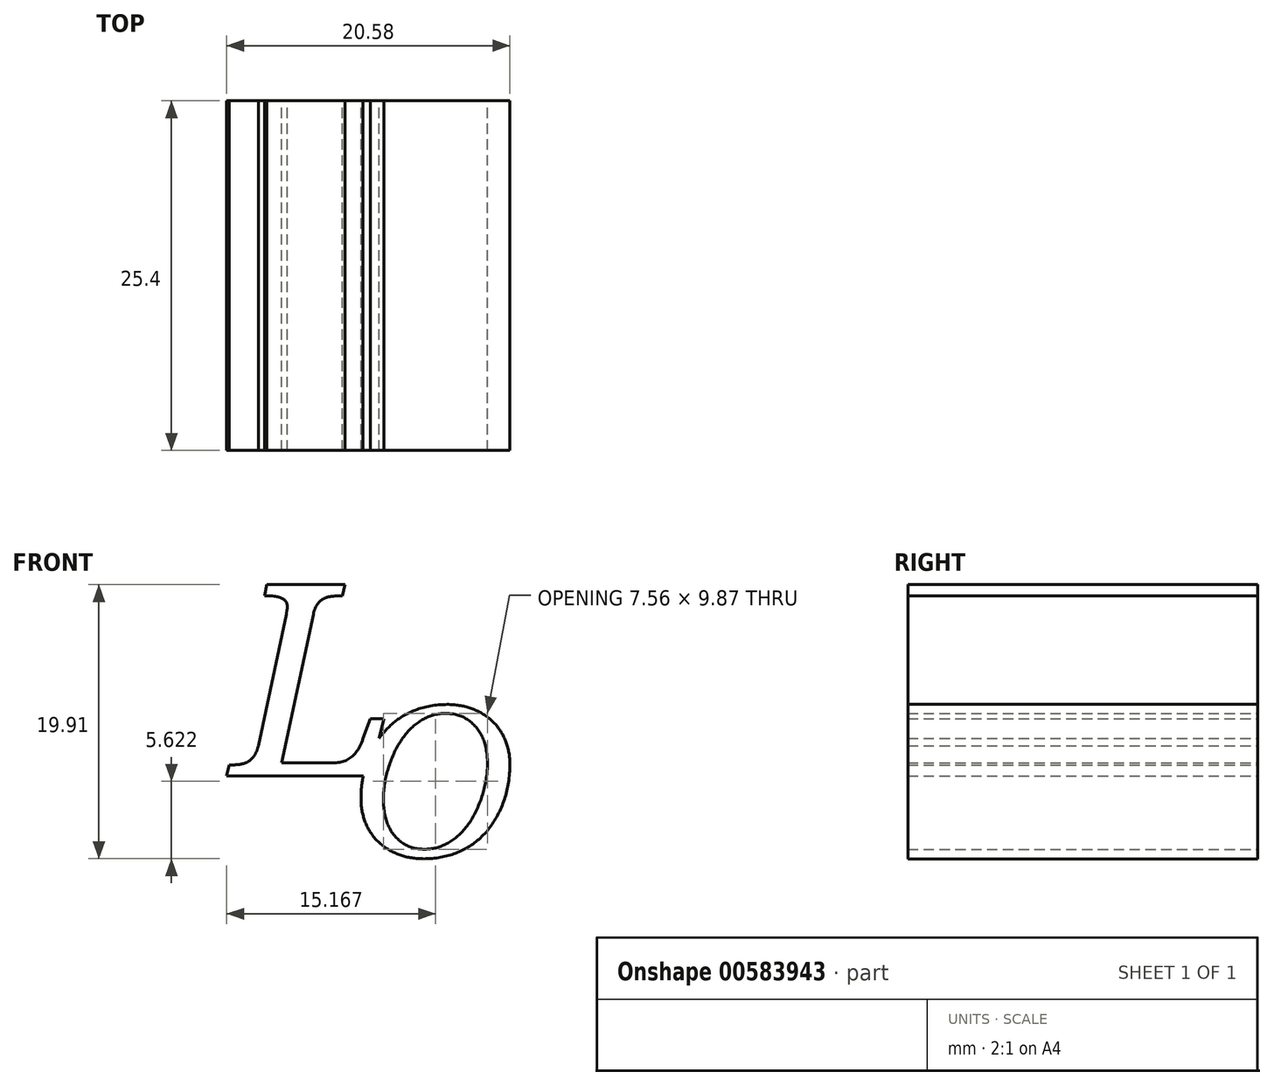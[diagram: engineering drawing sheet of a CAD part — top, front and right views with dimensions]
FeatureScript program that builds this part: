
annotation { "Feature Type Name" : "Feature", "Feature Type Description" : "" }
export const myFeature = defineFeature(function(context is Context, id is Id, definition is map)
    precondition{}
    {
        {
            var Q0;
            Q0=qCreatedBy(makeId("Front.planeOp"),FACE);
            var sketch = newSketch(context, id + "F0", { "sketchPlane" : qUnion([Q0])});
            skText(sketch, "E0", { "text": "L", "fontName": "NotoSerif-Italic.ttf"});
            const initialGuessF0  = {"E0": [-0.01286, -0.00168, 1, 0, 0.01403]};
            skSetInitialGuess(sketch, initialGuessF0);
            skSolve(sketch);
        }
        {
            var Q0;
            Q0=makeQuery(id+"F0.imprint","IMPRINT",FACE,{"disambiguationData":[TD([[makeQuery(id+"F0.imprint","IMPRINT",EDGE,{"derivedFrom":sQuery(id+"F0.wireOp",EDGE,"E0.sketch_text.stroke-0")}),-1.0]])]});
            var sketch = newSketch(context, id + "F1", { "sketchPlane" : qUnion([Q0])});
            skText(sketch, "E1", { "text": "O", "fontName": "Tinos-Italic.ttf"});
            const initialGuessF1  = {"E1": [-0.00433, -0.00752, 1, 0, 0.01201]};
            skSetInitialGuess(sketch, initialGuessF1);
            skSolve(sketch);
        }
        {
            var Q0;
            Q0=makeQuery(id+"F0.imprint","IMPRINT",FACE,{"disambiguationData":[TD([[makeQuery(id+"F0.imprint","IMPRINT",EDGE,{"derivedFrom":sQuery(id+"F0.wireOp",EDGE,"E0.sketch_text.stroke-0")}),-1.0]])]});
            extrude(context, id + "F2", {"entities" : qUnion([Q0]), "depth" : 25.4 * mm, "offsetDistance" : 25.4 * mm});
        }
        {
            var Q0;
            Q0=makeQuery(id+"F1.imprint","IMPRINT",FACE,{"disambiguationData":[TD([[makeQuery(id+"F1.imprint","IMPRINT",EDGE,{"derivedFrom":sQuery(id+"F1.wireOp",EDGE,"117566fc-86fc-4259-8c96-50a518b6edc2.sketch_text.stroke-0")}),-1.0]])]});
            var Q1;
            Q1 = qSketchRegion(id + "F0", true);
            extrude(context, id + "F3", {"entities" : qUnion([Q0, Q1]), "operationType" : NewBodyOperationType.ADD, "depth" : 25.4 * mm, "offsetDistance" : 25.4 * mm});
        }
        {
            var Q0;
            Q0=makeQuery(id+"F1.imprint","IMPRINT",FACE,{"disambiguationData":[TD([[makeQuery(id+"F1.imprint","IMPRINT",EDGE,{"derivedFrom":sQuery(id+"F1.wireOp",EDGE,"E1.sketch_text.stroke-0")}),-1.0]])]});
            extrude(context, id + "F4", {"entities" : qUnion([Q0]), "operationType" : NewBodyOperationType.ADD, "depth" : 25.4 * mm, "offsetDistance" : 25.4 * mm});
        }
    });
